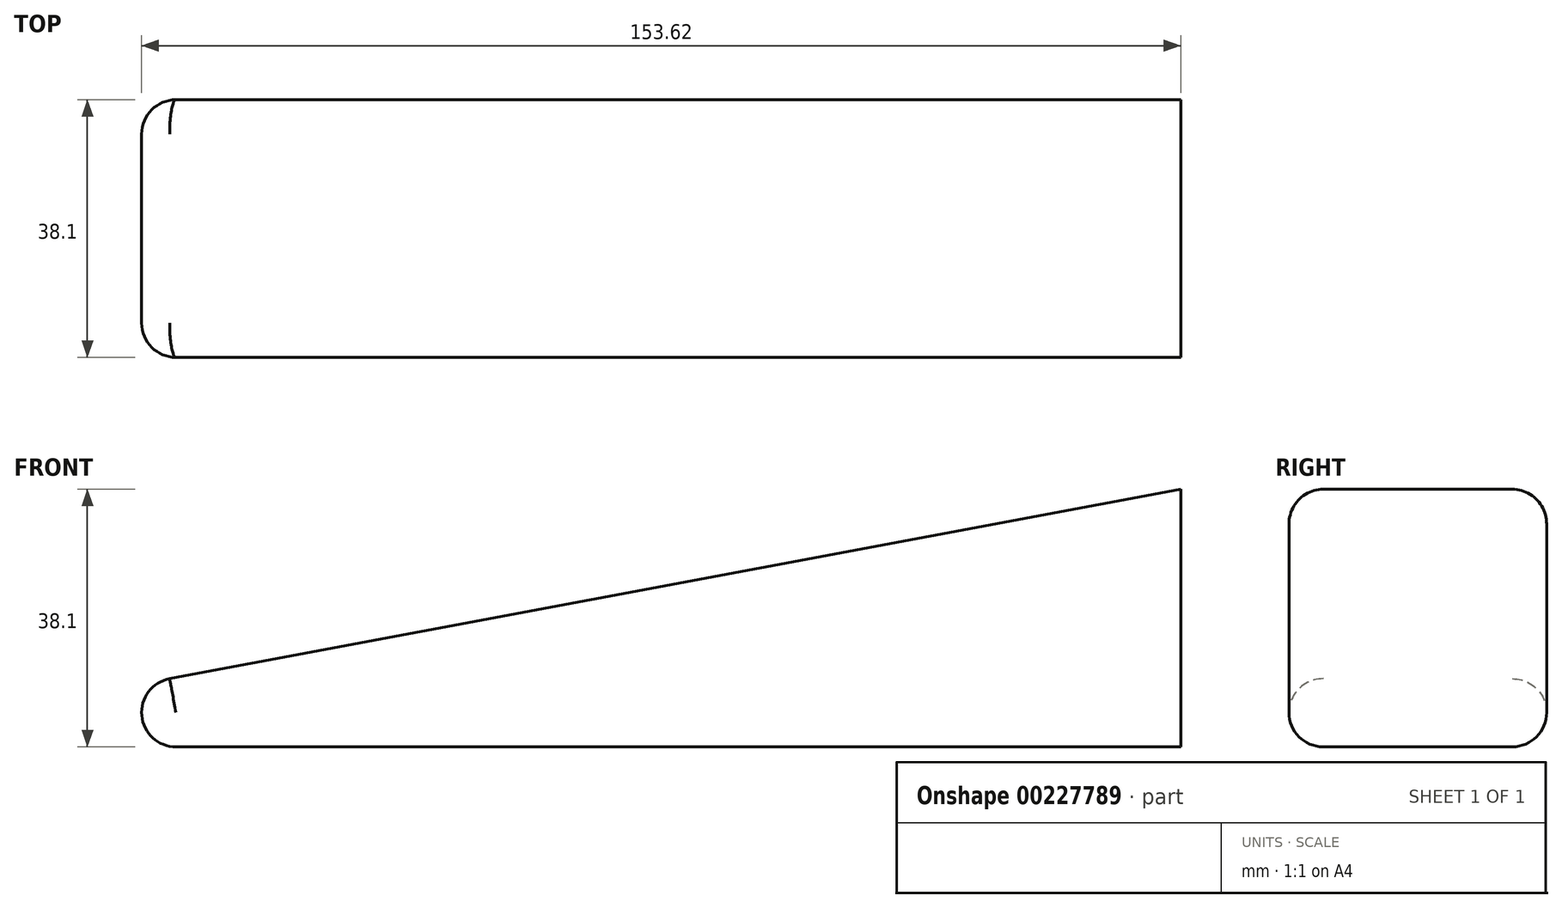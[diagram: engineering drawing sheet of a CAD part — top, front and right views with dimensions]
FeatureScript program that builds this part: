
annotation { "Feature Type Name" : "Feature", "Feature Type Description" : "" }
export const myFeature = defineFeature(function(context is Context, id is Id, definition is map)
    precondition{}
    {
        {
            var Q0;
            Q0=qCreatedBy(makeId("Front.planeOp"),FACE);
            var sketch = newSketch(context, id + "F0", { "sketchPlane" : qUnion([Q0])});
            skLineSegment(sketch, "E0", {"start": v(-101.86, 0) * mm, "end": v(101.34, 0) * mm});
            skLineSegment(sketch, "E1", {"start": v(101.34, 0) * mm, "end": v(101.34, 38.1) * mm});
            skLineSegment(sketch, "E2", {"start": v(101.34, 38.1) * mm, "end": v(-101.86, 0) * mm});
            skLineSegment(sketch, "E3", {"start": v(-101.86, 0) * mm, "end": v(-61.47, 0) * mm});
            skSolve(sketch);
        }
        {
            var Q0;
            Q0=makeQuery(id+"F0.imprint","IMPRINT",FACE,{"disambiguationData":[TD([[makeQuery(id+"F0.imprint","IMPRINT",EDGE,{"derivedFrom":sQuery(id+"F0.wireOp",EDGE,"E0")}),1.0]])]});
            extrude(context, id + "F1", {"entities" : qUnion([Q0]), "depth" : 38.1 * mm});
        }
        {
            var Q0;
            Q0=makeQuery(id+"F1.opExtrude","CAP_EDGE",EDGE,{"disambiguationData":[OSD([sQuery(id+"F0.wireOp",EDGE,"E2")])],"isStart":false});
            fillet(context, id + "F2", {"entities" : qUnion([Q0]), "radius" : 5.08 * mm, "tangentPropagation" : true, "allowEdgeOverflow" : false});
        }
        {
            var Q0;
            Q0=makeQuery(id+"F1.opExtrude","CAP_EDGE",EDGE,{"disambiguationData":[OSD([sQuery(id+"F0.wireOp",EDGE,"E2")])],"isStart":true});
            fillet(context, id + "F3", {"entities" : qUnion([Q0]), "radius" : 5.08 * mm, "tangentPropagation" : true, "allowEdgeOverflow" : false});
        }
        {
            var Q0;
            Q0=makeQuery(id+"F1.opExtrude","CAP_EDGE",EDGE,{"disambiguationData":[OSD([sQuery(id+"F0.wireOp",EDGE,"E0"),sQuery(id+"F0.wireOp",EDGE,"E3")])],"isStart":false});
            fillet(context, id + "F4", {"entities" : qUnion([Q0]), "radius" : 5.08 * mm, "tangentPropagation" : true, "allowEdgeOverflow" : false});
        }
    });
